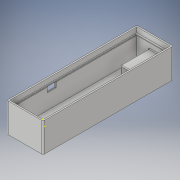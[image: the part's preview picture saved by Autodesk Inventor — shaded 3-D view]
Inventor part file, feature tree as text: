
AUTODESK INVENTOR PART (.ipt)
format: ipt  version: 2019 (Build 230136000, 136)  size: 245,760 bytes
history: native  units: mm
features: sketch x8, fillet x8, extrude x7, plane x2
ambient origin geometry x8: Origin, YZ Plane, XZ Plane, XY Plane, X Axis, Y Axis, Z Axis, Center Point
bodies: Body1 (feature_tree)
feature tree (25):
  sketch  "Sketch1"  dims[d0=47.0mm d1=179.0mm]
  extrude  "Extrusion3"  Depth=179.0mm
  extrude  "Extrusion4"  Depth=51.0mm
  sketch  "Sketch4"  dims[d4=2.5mm d6=51.0mm]
  extrude  "Extrusion6"  Depth=45.0mm
  extrude  "Extrusion7"  Depth=7.1mm TaperAngle=0.0deg
  extrude  "Extrusion8"  Depth=2.0mm TaperAngle=0.0deg
  plane  "Work Plane2"
  extrude  "Extrusion9"  Depth=40.0mm
  plane  "Work Plane1"
  extrude  "Extrusion10"  Depth=2.5mm
  fillet  "Fillet6"  Radius=19.0mm
  fillet  "Fillet7"  Radius=2.0mm
  fillet  "Fillet8"  Radius=7.0mm
  fillet  "Fillet9"  Radius=2.0mm
  fillet  "Fillet10"  Radius=11.5mm
  fillet  "Fillet11"  Radius=7.5mm
  fillet  "Fillet12"  Radius=2.0mm
  fillet  "Fillet13"  Radius=2.5mm
  sketch  "Sketch14"  dims[d51=1.0mm d52=1.0mm d53=1.0mm d54=1.0mm d55=0.5mm d56=0.5mm d57=2.0mm]
  sketch  "Sketch5"  dims[d7=183.0mm d15=45.0mm]
  sketch  "Sketch6"  dims[d16=174.0mm d17=7.1mm d18=32.0mm d19=0.0mm d20=0.0mm]
  sketch  "Sketch7"  dims[d21=1.0mm d22=0.0mm d29=2.0mm d30=0.0mm]
  sketch  "Sketch8"  dims[d31=28.0mm d32=40.0mm]
  sketch  "Sketch9"  dims[d33=30.0mm d34=40.0mm d35=19.0mm d36=0.0mm d37=2.0mm d38=0.0mm d39=7.0mm d40=2.0mm d41=0.0mm d42=11.5mm d43=7.5mm d44=2.0mm d45=0.0mm d50=2.5mm]
